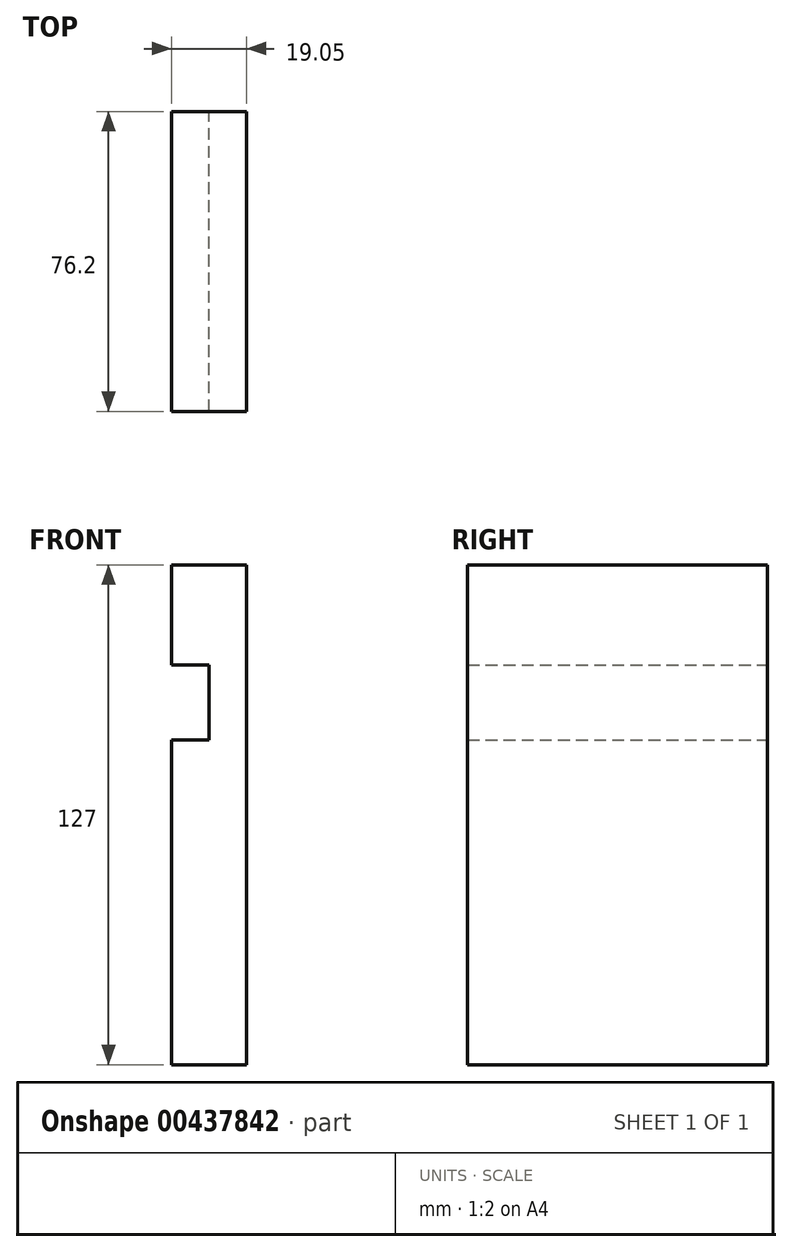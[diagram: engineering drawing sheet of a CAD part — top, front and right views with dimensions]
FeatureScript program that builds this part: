
annotation { "Feature Type Name" : "Feature", "Feature Type Description" : "" }
export const myFeature = defineFeature(function(context is Context, id is Id, definition is map)
    precondition{}
    {
        {
            var Q0;
            Q0=qCreatedBy(makeId("Front.planeOp"),FACE);
            var sketch = newSketch(context, id + "F0", { "sketchPlane" : qUnion([Q0])});
            skLineSegment(sketch, "E0", {"start": v(33.99, -64.77) * mm, "end": v(33.99, 62.23) * mm});
            skLineSegment(sketch, "E1", {"start": v(33.99, 62.23) * mm, "end": v(14.94, 62.23) * mm});
            skLineSegment(sketch, "E2", {"start": v(14.94, 62.23) * mm, "end": v(14.94, 36.83) * mm});
            skLineSegment(sketch, "E3", {"start": v(14.94, 36.83) * mm, "end": v(24.46, 36.83) * mm});
            skLineSegment(sketch, "E4", {"start": v(24.46, 36.83) * mm, "end": v(24.46, 17.78) * mm});
            skLineSegment(sketch, "E5", {"start": v(24.46, 17.78) * mm, "end": v(14.94, 17.78) * mm});
            skLineSegment(sketch, "E6", {"start": v(33.99, -64.77) * mm, "end": v(14.94, -64.77) * mm});
            skLineSegment(sketch, "E7", {"start": v(14.94, -64.77) * mm, "end": v(14.94, 17.78) * mm});
            skSolve(sketch);
        }
        {
            var Q0;
            Q0=makeQuery(id+"F0.imprint","IMPRINT",FACE,{"disambiguationData":[TD([[makeQuery(id+"F0.imprint","IMPRINT",EDGE,{"derivedFrom":sQuery(id+"F0.wireOp",EDGE,"E0")}),1.0]])]});
            extrude(context, id + "F1", {"entities" : qUnion([Q0]), "depth" : 76.2 * mm});
        }
    });
